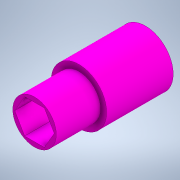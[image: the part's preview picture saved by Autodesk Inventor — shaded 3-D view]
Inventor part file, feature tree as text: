
AUTODESK INVENTOR PART (.ipt)
format: ipt  version: 2022.1 (Build 261234000, 234)  size: 139,264 bytes
history: native  units: in
note: dims shown in document units (in); Inventor stores cm internally (conversion verified against a paired STEP export)
features: extrude x2, sketch x2, other x1, thicken_offset x1
ambient origin geometry x8: Origin, YZ Plane, XZ Plane, XY Plane, X Axis, Y Axis, Z Axis, Center Point
bodies: Solid1 (feature_tree)
feature tree (6):
  extrude  "Extrusion1"  Depth=0.625in
  other  "Thicken Hex"
  extrude  "Extrusion2"  Depth=0.75in TaperAngle=0.0deg
  thicken_offset  "Thicken2"
  sketch  "Sketch1"  dims[d0=0.375in d2=0.625in]
  sketch  "Sketch3"  dims[d3=0.096in d4=0.75in d5=0.0in d6=0.005in d7=0.005in d8=0.5in d9=0.0in d10=0.5in d11=0.005in d12=0.005in]
